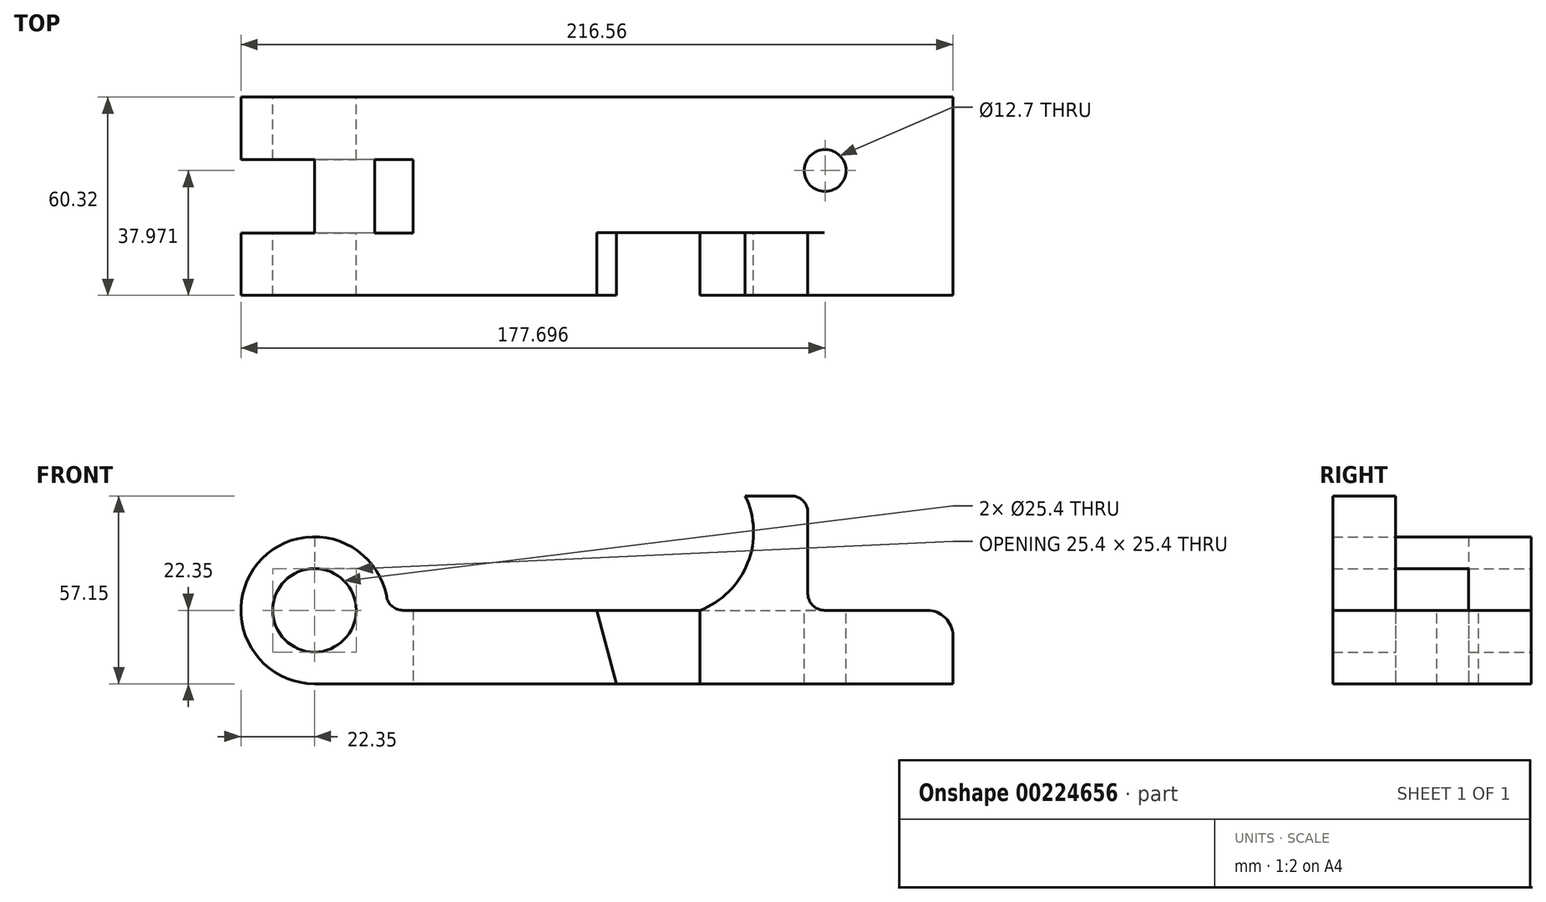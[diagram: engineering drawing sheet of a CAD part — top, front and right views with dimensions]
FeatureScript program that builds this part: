
annotation { "Feature Type Name" : "Feature", "Feature Type Description" : "" }
export const myFeature = defineFeature(function(context is Context, id is Id, definition is map)
    precondition{}
    {
        {
            var Q0;
            Q0=qCreatedBy(makeId("Front.planeOp"),FACE);
            var sketch = newSketch(context, id + "F0", { "sketchPlane" : qUnion([Q0])});
            skCircle(sketch, "E0", {"center": v(0, 0) * mm, "radius": 12.7 * mm});
            skArc(sketch, "E1", {"start": v(0, -22.35) * mm, "mid": v(-15.8, 15.8) * mm, "end": v(22.35, 0) * mm});
            skLineSegment(sketch, "E2", {"start": v(0, -22.35) * mm, "end": v(91.85, -22.35) * mm});
            skLineSegment(sketch, "E3", {"start": v(0, 0) * mm, "end": v(85.85, 0) * mm});
            skLineSegment(sketch, "E4", {"start": v(85.85, 0) * mm, "end": v(91.85, -22.35) * mm});
            skLineSegment(sketch, "E5", {"start": v(0, -22.35) * mm, "end": v(117.25, -22.35) * mm});
            skLineSegment(sketch, "E6", {"start": v(117.25, -22.35) * mm, "end": v(117.25, 0) * mm});
            skLineSegment(sketch, "E7", {"start": v(117.25, 0) * mm, "end": v(85.85, 0) * mm});
            skLineSegment(sketch, "E8", {"start": v(0, -22.35) * mm, "end": v(194.2, -22.35) * mm});
            skLineSegment(sketch, "E9", {"start": v(194.2, -22.35) * mm, "end": v(194.2, 0) * mm});
            skLineSegment(sketch, "E10", {"start": v(194.2, 0) * mm, "end": v(150.09, 0) * mm});
            skLineSegment(sketch, "E11", {"start": v(150.09, 0) * mm, "end": v(150.09, 34.8) * mm});
            skLineSegment(sketch, "E12", {"start": v(150.09, 34.8) * mm, "end": v(131.04, 34.8) * mm});
            skCircle(sketch, "E13", {"center": v(108.18, 23.73) * mm, "radius": 25.4 * mm});
            skPoint(sketch, "E13.first.point", {"position": v(82.78, 23.73) * mm});
            skLineSegment(sketch, "E14", {"start": v(117.25, 0) * mm, "end": v(150.09, 0) * mm});
            skSolve(sketch);
        }
        {
            var Q0;
            Q0=makeQuery(id+"F0.imprint","IMPRINT",FACE,{"disambiguationData":[TD([[makeQuery(id+"F0.imprint","IMPRINT",EDGE,{"derivedFrom":sQuery(id+"F0.wireOp",EDGE,"E0")}),-1.0]])]});
            var Q1;
            {var subQ1=sQuery(id+"F0.wireOp",EDGE,"E4");Q1=makeQuery(id+"F0.imprint","IMPRINT",FACE,{"disambiguationData":[TD([[makeQuery(id+"F0.imprint","IMPRINT",EDGE,{"derivedFrom":subQ1}),1.0]])]});}
            var Q2;
            {var subQ0=sQuery(id+"F0.wireOp",EDGE,"E13");var subQ1=sQuery(id+"F0.wireOp",EDGE,"E7");var subQ3=makeQuery(id+"F0.imprint","INTERSECT",VERTEX,{"derivedFrom":[subQ1,subQ0]});Q2=makeQuery(id+"F0.imprint","IMPRINT",FACE,{"disambiguationData":[TD([[makeQuery(id+"F0.imprint","IMPRINT",EDGE,{"disambiguationData":[TD([[subQ3,1.0]])],"derivedFrom":subQ1}),1.0]])]});}
            var Q3;
            {var subQ2=sQuery(id+"F0.wireOp",EDGE,"E6");Q3=makeQuery(id+"F0.imprint","IMPRINT",FACE,{"disambiguationData":[TD([[makeQuery(id+"F0.imprint","IMPRINT",EDGE,{"derivedFrom":subQ2}),-1.0]])]});}
            var Q4;
            Q4=makeQuery(id+"F0.imprint","IMPRINT",FACE,{"disambiguationData":[TD([[makeQuery(id+"F0.imprint","IMPRINT",EDGE,{"derivedFrom":sQuery(id+"F0.wireOp",EDGE,"E11")}),1.0]])]});
            extrude(context, id + "F1", {"entities" : qUnion([Q0, Q1, Q2, Q3, Q4]), "depth" : 30.16 * mm});
        }
        {
            var Q0;
            {var subQ2=sQuery(id+"F0.wireOp",EDGE,"E6");Q0=makeQuery(id+"F0.imprint","IMPRINT",FACE,{"disambiguationData":[TD([[makeQuery(id+"F0.imprint","IMPRINT",EDGE,{"derivedFrom":subQ2}),-1.0]])]});}
            extrude(context, id + "F2", {"entities" : qUnion([Q0]), "operationType" : NewBodyOperationType.ADD, "oppositeDirection" : true, "depth" : 30.16 * mm});
        }
        {
            var Q0;
            {var subQ0=sQuery(id+"F0.wireOp",EDGE,"E7");var subQ1=sQuery(id+"F0.wireOp",EDGE,"E3");var subQ2=sQuery(id+"F0.wireOp",EDGE,"E8");var subQ3=sQuery(id+"F0.wireOp",EDGE,"E1");var subQ4=sQuery(id+"F0.wireOp",EDGE,"E13");var subQ5=sQuery(id+"F0.wireOp",EDGE,"E10");var subQ6=sQuery(id+"F0.wireOp",EDGE,"E0");var subQ7=makeQuery(id+"F1.opExtrude","CAP_FACE",FACE,{"disambiguationData":[OSD([subQ6,subQ3,subQ1,subQ0,subQ2,sQuery(id+"F0.wireOp",EDGE,"E9"),subQ5,sQuery(id+"F0.wireOp",EDGE,"E11"),sQuery(id+"F0.wireOp",EDGE,"E12"),subQ4])],"isStart":true});Q0=makeQuery(id+"F2.boolean.opBoolean","SPLIT",FACE,{"disambiguationData":[TD([makeQuery(id+"F1.opExtrude","SWEPT_FACE",FACE,{"disambiguationData":[OSD([subQ6])]})])],"derivedFrom":subQ7});}
            extrude(context, id + "F3", {"entities" : qUnion([Q0]), "operationType" : NewBodyOperationType.ADD, "depth" : 30.16 * mm});
        }
        {
            var Q0;
            Q0=makeQuery(id+"F1.opExtrude","CAP_FACE",FACE,{"disambiguationData":[OSD([sQuery(id+"F0.wireOp",EDGE,"E0"),sQuery(id+"F0.wireOp",EDGE,"E1"),sQuery(id+"F0.wireOp",EDGE,"E3"),sQuery(id+"F0.wireOp",EDGE,"E7"),sQuery(id+"F0.wireOp",EDGE,"E8"),sQuery(id+"F0.wireOp",EDGE,"E9"),sQuery(id+"F0.wireOp",EDGE,"E10"),sQuery(id+"F0.wireOp",EDGE,"E11"),sQuery(id+"F0.wireOp",EDGE,"E12"),sQuery(id+"F0.wireOp",EDGE,"E13")])],"isStart":false});
            var sketch = newSketch(context, id + "F4", { "sketchPlane" : qUnion([Q0])});
            skLineSegment(sketch, "E15", {"start": v(0, -22.35) * mm, "end": v(91.85, -22.35) * mm});
            skLineSegment(sketch, "E16", {"start": v(0, 0) * mm, "end": v(85.85, 0) * mm});
            skLineSegment(sketch, "E17", {"start": v(85.85, 0) * mm, "end": v(91.85, -22.35) * mm});
            skLineSegment(sketch, "E18", {"start": v(0, 0) * mm, "end": v(117.25, 0) * mm});
            skLineSegment(sketch, "E19", {"start": v(117.25, 0) * mm, "end": v(117.25, -22.35) * mm});
            skLineSegment(sketch, "E20", {"start": v(117.25, -22.35) * mm, "end": v(91.85, -22.35) * mm});
            skSolve(sketch);
        }
        {
            var Q0;
            {var subQ0=sQuery(id+"F4.wireOp",EDGE,"E17");Q0=makeQuery(id+"F4.imprint","IMPRINT",FACE,{"disambiguationData":[TD([[makeQuery(id+"F4.imprint","IMPRINT",EDGE,{"derivedFrom":subQ0}),1.0]])]});}
            extrude(context, id + "F5", {"entities" : qUnion([Q0]), "operationType" : NewBodyOperationType.REMOVE, "oppositeDirection" : true, "depth" : 19.05 * mm});
        }
        {
            var Q0;
            Q0=makeQuery(id+"F1.opExtrude","SWEPT_FACE",FACE,{"disambiguationData":[OSD([sQuery(id+"F0.wireOp",EDGE,"E11")])]});
            var sketch = newSketch(context, id + "F6", { "sketchPlane" : qUnion([Q0])});
            skLineSegment(sketch, "E21", {"start": v(-30.16, 34.8) * mm, "end": v(-11.11, 34.8) * mm});
            skLineSegment(sketch, "E22", {"start": v(-11.11, 34.8) * mm, "end": v(-11.11, 0) * mm});
            skLineSegment(sketch, "E23", {"start": v(-11.11, 0) * mm, "end": v(-30.16, 0) * mm});
            skLineSegment(sketch, "E24", {"start": v(-30.16, 0) * mm, "end": v(-30.16, 34.8) * mm});
            skSolve(sketch);
        }
        {
            var Q0;
            {var subQ0=sQuery(id+"F6.wireOp",EDGE,"E22");Q0=makeQuery(id+"F6.imprint","IMPRINT",FACE,{"disambiguationData":[TD([[makeQuery(id+"F6.imprint","IMPRINT",EDGE,{"derivedFrom":subQ0}),1.0]])]});}
            extrude(context, id + "F7", {"entities" : qUnion([Q0]), "operationType" : NewBodyOperationType.REMOVE, "oppositeDirection" : true, "depth" : 50.8 * mm});
        }
        {
            var Q0;
            {var subQ0=sQuery(id+"F0.wireOp",EDGE,"E14");var subQ1=sQuery(id+"F0.wireOp",EDGE,"E10");var subQ2=sQuery(id+"F0.wireOp",EDGE,"E7");var subQ3=sQuery(id+"F0.wireOp",EDGE,"E3");Q0=makeQuery(id+"F7.boolean.opBoolean","MERGE",FACE,{"derivedFrom":[makeQuery(id+"F3.boolean.opBoolean","MERGE",FACE,{"derivedFrom":[makeQuery(id+"F1.opExtrude","SWEPT_FACE",FACE,{"disambiguationData":[OSD([subQ3,subQ2])]}),makeQuery(id+"F2.boolean.opBoolean","MERGE",FACE,{"derivedFrom":[makeQuery(id+"F1.opExtrude","SWEPT_FACE",FACE,{"disambiguationData":[OSD([subQ1])]}),makeQuery(id+"F2.opExtrude","SWEPT_FACE",FACE,{"disambiguationData":[OSD([subQ1,subQ0])]})]}),makeQuery(id+"F3.opExtrude","SWEPT_FACE",FACE,{"disambiguationData":[OSD([subQ3,subQ2])]})]}),makeQuery(id+"F7.opExtrude","SWEPT_FACE",FACE,{"disambiguationData":[OSD([subQ1,sQuery(id+"F0.wireOp",EDGE,"E11"),subQ0])]})]});}
            var sketch = newSketch(context, id + "F8", { "sketchPlane" : qUnion([Q0])});
            skLineSegment(sketch, "E25", {"start": v(194.2, 30.16) * mm, "end": v(155.35, 30.16) * mm});
            skLineSegment(sketch, "E26", {"start": v(155.35, 30.16) * mm, "end": v(155.35, 7.81) * mm});
            skCircle(sketch, "E27", {"center": v(155.35, 7.81) * mm, "radius": 6.35 * mm});
            skSolve(sketch);
        }
        {
            var Q0;
            Q0=makeQuery(id+"F8.imprint","IMPRINT",FACE,{"disambiguationData":[TD([[makeQuery(id+"F8.imprint","IMPRINT",EDGE,{"derivedFrom":sQuery(id+"F8.wireOp",EDGE,"E27")}),1.0]])]});
            extrude(context, id + "F9", {"entities" : qUnion([Q0]), "operationType" : NewBodyOperationType.REMOVE, "oppositeDirection" : true, "depth" : 50.8 * mm});
        }
        {
            var Q0;
            {var subQ0=sQuery(id+"F0.wireOp",EDGE,"E10");var subQ1=sQuery(id+"F0.wireOp",EDGE,"E9");Q0=makeQuery(id+"F2.boolean.opBoolean","MERGE",EDGE,{"derivedFrom":[makeQuery(id+"F1.opExtrude","SWEPT_EDGE",EDGE,{"disambiguationData":[OSD([subQ1,subQ0])]}),makeQuery(id+"F2.opExtrude","SWEPT_EDGE",EDGE,{"disambiguationData":[OSD([subQ1,subQ0])]})]});}
            fillet(context, id + "F10", {"entities" : qUnion([Q0]), "radius" : 7.87 * mm, "tangentPropagation" : true, "allowEdgeOverflow" : false});
        }
        {
            var Q0;
            Q0=makeQuery(id+"F1.opExtrude","SWEPT_EDGE",EDGE,{"disambiguationData":[OSD([sQuery(id+"F0.wireOp",EDGE,"E11"),sQuery(id+"F0.wireOp",EDGE,"E12")])]});
            fillet(context, id + "F11", {"entities" : qUnion([Q0]), "radius" : 5.08 * mm, "tangentPropagation" : true, "allowEdgeOverflow" : false});
        }
        {
            var Q0;
            {var subQ0=sQuery(id+"F0.wireOp",EDGE,"E3");var subQ1=sQuery(id+"F0.wireOp",EDGE,"E1");Q0=makeQuery(id+"F3.boolean.opBoolean","MERGE",EDGE,{"derivedFrom":[makeQuery(id+"F1.opExtrude","SWEPT_EDGE",EDGE,{"disambiguationData":[OSD([subQ1,subQ0])]}),makeQuery(id+"F3.opExtrude","SWEPT_EDGE",EDGE,{"disambiguationData":[OSD([subQ1,subQ0])]})]});}
            fillet(context, id + "F12", {"entities" : qUnion([Q0]), "radius" : 5.08 * mm, "tangentPropagation" : true, "allowEdgeOverflow" : false});
        }
        {
            var Q0;
            Q0=makeQuery(id+"F1.opExtrude","SWEPT_EDGE",EDGE,{"disambiguationData":[OSD([sQuery(id+"F0.wireOp",EDGE,"E10"),sQuery(id+"F0.wireOp",EDGE,"E11"),sQuery(id+"F0.wireOp",EDGE,"E14")])]});
            fillet(context, id + "F13", {"entities" : qUnion([Q0]), "radius" : 5.08 * mm, "tangentPropagation" : true, "allowEdgeOverflow" : false});
        }
        {
            var Q0;
            {var subQ0=sQuery(id+"F0.wireOp",EDGE,"E8");Q0=makeQuery(id+"F3.boolean.opBoolean","MERGE",FACE,{"derivedFrom":[makeQuery(id+"F2.boolean.opBoolean","MERGE",FACE,{"derivedFrom":[makeQuery(id+"F1.opExtrude","SWEPT_FACE",FACE,{"disambiguationData":[OSD([subQ0])]}),makeQuery(id+"F2.opExtrude","SWEPT_FACE",FACE,{"disambiguationData":[OSD([subQ0])]})]}),makeQuery(id+"F3.opExtrude","SWEPT_FACE",FACE,{"disambiguationData":[OSD([subQ0])]})]});}
            var sketch = newSketch(context, id + "F14", { "sketchPlane" : qUnion([Q0])});
            skLineSegment(sketch, "E28", {"start": v(0, -30.16) * mm, "end": v(0, -11.16) * mm});
            skLineSegment(sketch, "E29", {"start": v(0, 30.16) * mm, "end": v(0, 11.16) * mm});
            skLineSegment(sketch, "E30.bottom", {"start": v(0, -11.16) * mm, "end": v(-51.43, -11.16) * mm});
            skLineSegment(sketch, "E30.top", {"start": v(0, 11.16) * mm, "end": v(-51.43, 11.16) * mm});
            skLineSegment(sketch, "E30.left", {"start": v(0, -11.16) * mm, "end": v(0, 11.16) * mm});
            skLineSegment(sketch, "E30.right", {"start": v(-51.43, -11.16) * mm, "end": v(-51.43, 11.16) * mm});
            skSolve(sketch);
        }
        {
            var Q0;
            Q0=makeQuery(id+"F14.imprint","IMPRINT",FACE,{"disambiguationData":[TD([[makeQuery(id+"F14.imprint","IMPRINT",EDGE,{"derivedFrom":sQuery(id+"F14.wireOp",EDGE,"E30.bottom")}),-1.0]])]});
            extrude(context, id + "F15", {"entities" : qUnion([Q0]), "operationType" : NewBodyOperationType.REMOVE, "oppositeDirection" : true, "depth" : 50.8 * mm});
        }
        {
            var Q0;
            {var subQ0=sQuery(id+"F0.wireOp",EDGE,"E1");var subQ1=sQuery(id+"F0.wireOp",EDGE,"E0");Q0=makeQuery(id+"F15.boolean.opBoolean","COPY",FACE,{"disambiguationData":[TD([makeQuery(id+"F1.opExtrude","SWEPT_FACE",FACE,{"disambiguationData":[OSD([subQ1])]}),makeQuery(id+"F1.opExtrude","SWEPT_FACE",FACE,{"disambiguationData":[OSD([subQ0])]}),makeQuery(id+"F3.opExtrude","SWEPT_FACE",FACE,{"disambiguationData":[OSD([subQ1])]}),makeQuery(id+"F3.opExtrude","SWEPT_FACE",FACE,{"disambiguationData":[OSD([subQ0])]}),makeQuery(id+"F15.opExtrude","SWEPT_FACE",FACE,{"disambiguationData":[OSD([sQuery(id+"F14.wireOp",EDGE,"E30.bottom")])]}),makeQuery(id+"F15.opExtrude","SWEPT_FACE",FACE,{"disambiguationData":[OSD([sQuery(id+"F14.wireOp",EDGE,"E30.top")])]})])],"derivedFrom":makeQuery(id+"F15.opExtrude","SWEPT_FACE",FACE,{"disambiguationData":[OSD([sQuery(id+"F14.wireOp",EDGE,"E30.left")])]})});}
            var sketch = newSketch(context, id + "F16", { "sketchPlane" : qUnion([Q0])});
            skLineSegment(sketch, "E31.bottom", {"start": v(-11.16, 22.35) * mm, "end": v(11.16, 22.35) * mm});
            skLineSegment(sketch, "E31.top", {"start": v(-11.16, 0) * mm, "end": v(11.16, 0) * mm});
            skLineSegment(sketch, "E31.left", {"start": v(-11.16, 22.35) * mm, "end": v(-11.16, 0) * mm});
            skLineSegment(sketch, "E31.right", {"start": v(11.16, 22.35) * mm, "end": v(11.16, 0) * mm});
            skSolve(sketch);
        }
        {
            var Q0;
            {var subQ0=sQuery(id+"F16.wireOp",EDGE,"E31.bottom");Q0=makeQuery(id+"F16.imprint","IMPRINT",FACE,{"disambiguationData":[TD([[makeQuery(id+"F16.imprint","IMPRINT",EDGE,{"derivedFrom":subQ0}),-1.0]])]});}
            var Q1;
            {var subQ0=sQuery(id+"F16.wireOp",EDGE,"E31.top");Q1=makeQuery(id+"F16.imprint","IMPRINT",FACE,{"disambiguationData":[TD([[makeQuery(id+"F16.imprint","IMPRINT",EDGE,{"derivedFrom":subQ0}),1.0]])]});}
            extrude(context, id + "F17", {"entities" : qUnion([Q0, Q1]), "operationType" : NewBodyOperationType.REMOVE, "oppositeDirection" : true, "depth" : 25.4 * mm});
        }
        {
            var Q0;
            Q0=makeQuery(id+"F17.boolean.opBoolean","COPY",FACE,{"derivedFrom":makeQuery(id+"F17.opExtrude","SWEPT_FACE",FACE,{"disambiguationData":[OSD([sQuery(id+"F16.wireOp",EDGE,"E31.top")])]})});
            extrude(context, id + "F18", {"entities" : qUnion([Q0]), "operationType" : NewBodyOperationType.REMOVE, "oppositeDirection" : true, "depth" : 50.8 * mm});
        }
        {
            var Q0;
            {var subQ0=sQuery(id+"F0.wireOp",EDGE,"E8");Q0=makeQuery(id+"F3.boolean.opBoolean","MERGE",FACE,{"derivedFrom":[makeQuery(id+"F2.boolean.opBoolean","MERGE",FACE,{"derivedFrom":[makeQuery(id+"F1.opExtrude","SWEPT_FACE",FACE,{"disambiguationData":[OSD([subQ0])]}),makeQuery(id+"F2.opExtrude","SWEPT_FACE",FACE,{"disambiguationData":[OSD([subQ0])]})]}),makeQuery(id+"F3.opExtrude","SWEPT_FACE",FACE,{"disambiguationData":[OSD([subQ0])]})]});}
            var sketch = newSketch(context, id + "F19", { "sketchPlane" : qUnion([Q0])});
            skLineSegment(sketch, "E32.bottom", {"start": v(12.7, 11.16) * mm, "end": v(0, 11.16) * mm});
            skLineSegment(sketch, "E32.top", {"start": v(12.7, -11.16) * mm, "end": v(0, -11.16) * mm});
            skLineSegment(sketch, "E32.left", {"start": v(12.7, 11.16) * mm, "end": v(12.7, -11.16) * mm});
            skLineSegment(sketch, "E32.right", {"start": v(0, 11.16) * mm, "end": v(0, -11.16) * mm});
            skSolve(sketch);
        }
        {
            var Q0;
            Q0=makeQuery(id+"F19.imprint","IMPRINT",FACE,{"disambiguationData":[TD([[makeQuery(id+"F19.imprint","IMPRINT",EDGE,{"derivedFrom":sQuery(id+"F19.wireOp",EDGE,"E32.bottom")}),1.0]])]});
            extrude(context, id + "F20", {"entities" : qUnion([Q0]), "operationType" : NewBodyOperationType.REMOVE, "oppositeDirection" : true, "depth" : 25.4 * mm});
        }
        {
            var Q0;
            {var subQ0=sQuery(id+"F0.wireOp",EDGE,"E8");Q0=makeQuery(id+"F3.boolean.opBoolean","MERGE",FACE,{"derivedFrom":[makeQuery(id+"F2.boolean.opBoolean","MERGE",FACE,{"derivedFrom":[makeQuery(id+"F1.opExtrude","SWEPT_FACE",FACE,{"disambiguationData":[OSD([subQ0])]}),makeQuery(id+"F2.opExtrude","SWEPT_FACE",FACE,{"disambiguationData":[OSD([subQ0])]})]}),makeQuery(id+"F3.opExtrude","SWEPT_FACE",FACE,{"disambiguationData":[OSD([subQ0])]})]});}
            var sketch = newSketch(context, id + "F21", { "sketchPlane" : qUnion([Q0])});
            skLineSegment(sketch, "E33.bottom", {"start": v(25.4, 11.16) * mm, "end": v(30.02, 11.16) * mm});
            skLineSegment(sketch, "E33.top", {"start": v(25.4, -11.16) * mm, "end": v(30.02, -11.16) * mm});
            skLineSegment(sketch, "E33.left", {"start": v(25.4, 11.16) * mm, "end": v(25.4, -11.16) * mm});
            skLineSegment(sketch, "E33.right", {"start": v(30.02, 11.16) * mm, "end": v(30.02, -11.16) * mm});
            skSolve(sketch);
        }
        {
            var Q0;
            Q0 = qSketchRegion(id + "F21", true);
            extrude(context, id + "F22", {"entities" : qUnion([Q0]), "operationType" : NewBodyOperationType.REMOVE, "oppositeDirection" : true, "depth" : 25.4 * mm});
        }
    });
